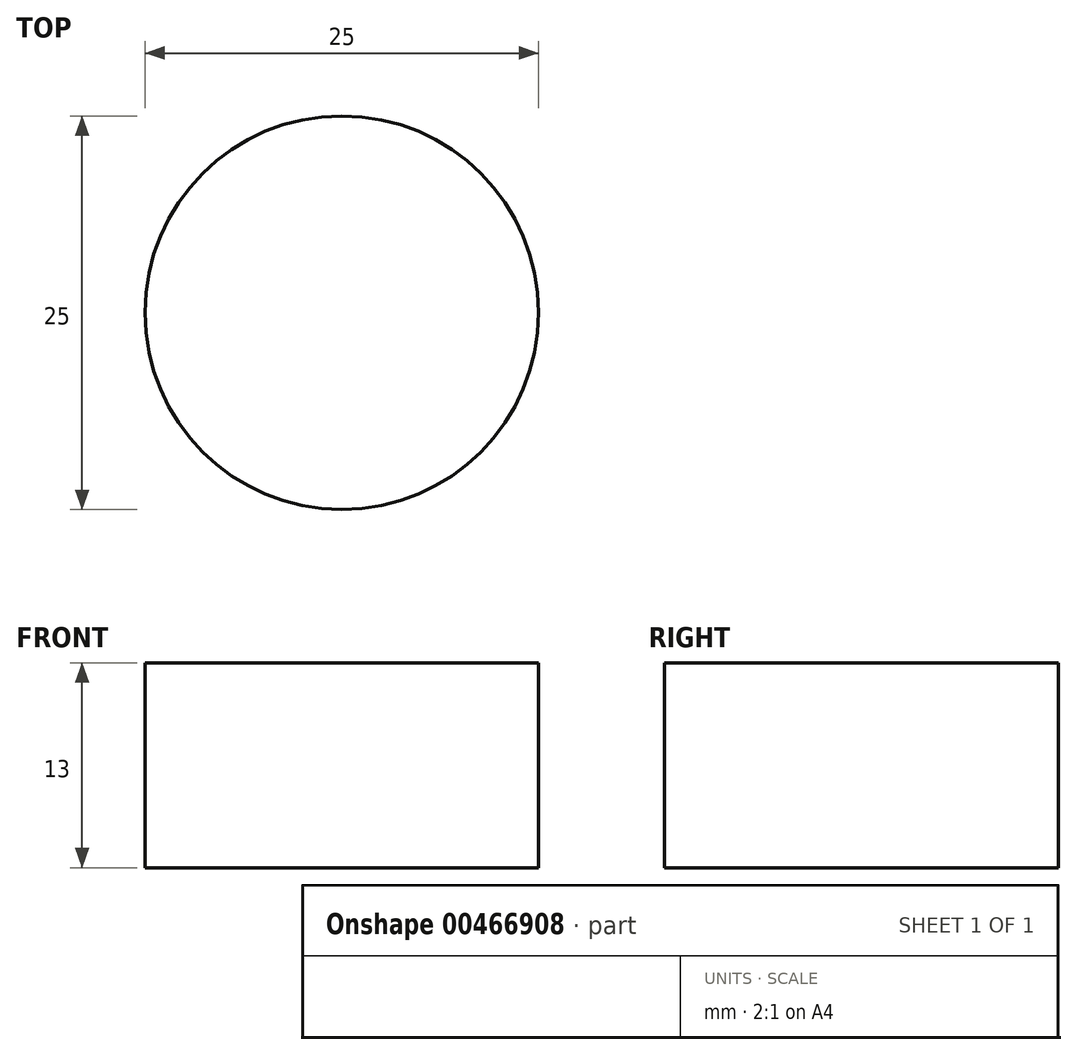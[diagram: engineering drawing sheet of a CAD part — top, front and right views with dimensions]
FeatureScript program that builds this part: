
annotation { "Feature Type Name" : "Feature", "Feature Type Description" : "" }
export const myFeature = defineFeature(function(context is Context, id is Id, definition is map)
    precondition{}
    {
        {
            var Q0;
            Q0=qCreatedBy(makeId("Top.planeOp"),FACE);
            var sketch = newSketch(context, id + "F0", { "sketchPlane" : qUnion([Q0])});
            skCircle(sketch, "E0", {"center": v(0, 0) * mm, "radius": 12.5 * mm});
            skSolve(sketch);
        }
        {
            var Q0;
            Q0=makeQuery(id+"F0.imprint","IMPRINT",FACE,{"disambiguationData":[TD([[makeQuery(id+"F0.imprint","IMPRINT",EDGE,{"derivedFrom":sQuery(id+"F0.wireOp",EDGE,"E0")}),1.0]])]});
            extrude(context, id + "F1", {"entities" : qUnion([Q0]), "depth" : 13 * mm});
        }
    });
